# Revit family: Sink-Undermount-Kitchen-KALLISTA-Bacifiore-L20308
name_source: partatom
category: Plumbing Fixtures
units: mm (PartAtom-declared; Revit-internal decimal feet)

## family parameters
Cut with Voids When Loaded = No
Host = Face
Maintain Annotation Orientation = No
OmniClass Number = 23.31.13.00
Part Type = Normal
Room Calculation Point = No
Round Connector Dimension = Use Diameter
Shared = No

## types (2) — shared parameters
ADA Compliant = No
Assembly Code = D2010400
CW Connection = No
Cold Water Inlet = Cold Water Inlet
Date Modified = 04/29/2025
Default Elevation = 36"
Description = Bacifiore Entertrainment Sink
Drain Included = Yes
HW Connection = No
Height = 7"
Hot Water Inlet = Hot Water Inlet
Length = 18"
Manufacturer = Kohler Co.
Master Format 2014 = 22 41 16
Master Format 2014 Name = Residential Lavatories and Sinks
Material = Premium Metal Construction
Product Documentation Link = https://www.us.kohler.com
Product Name = Bacifiore
Product Page URL = http://www.us.kohler.com
URL = https://www.us.kohler.com
Vent Connection = No
Waste Connection = Yes
Waste Water Outlet = Waste Water Outlet
WaterSense Certified = No
Width = 18"

## per-type parameters (varying)
| type | Finish | Model | Type |
| NA-Stainless_Steel | Kallista-Metal-SS-Stainless_Steel | L20308-00-NA | 1 |
| PDS-Polished Distressed Steel | Kallista-Metal-PDS-Polished_Distressed_Steel | L20308-00-PDS | 2 |

## geometry (parser evidence)
native form markers: Sweep x5
no freeform markers — native parametric forms only
